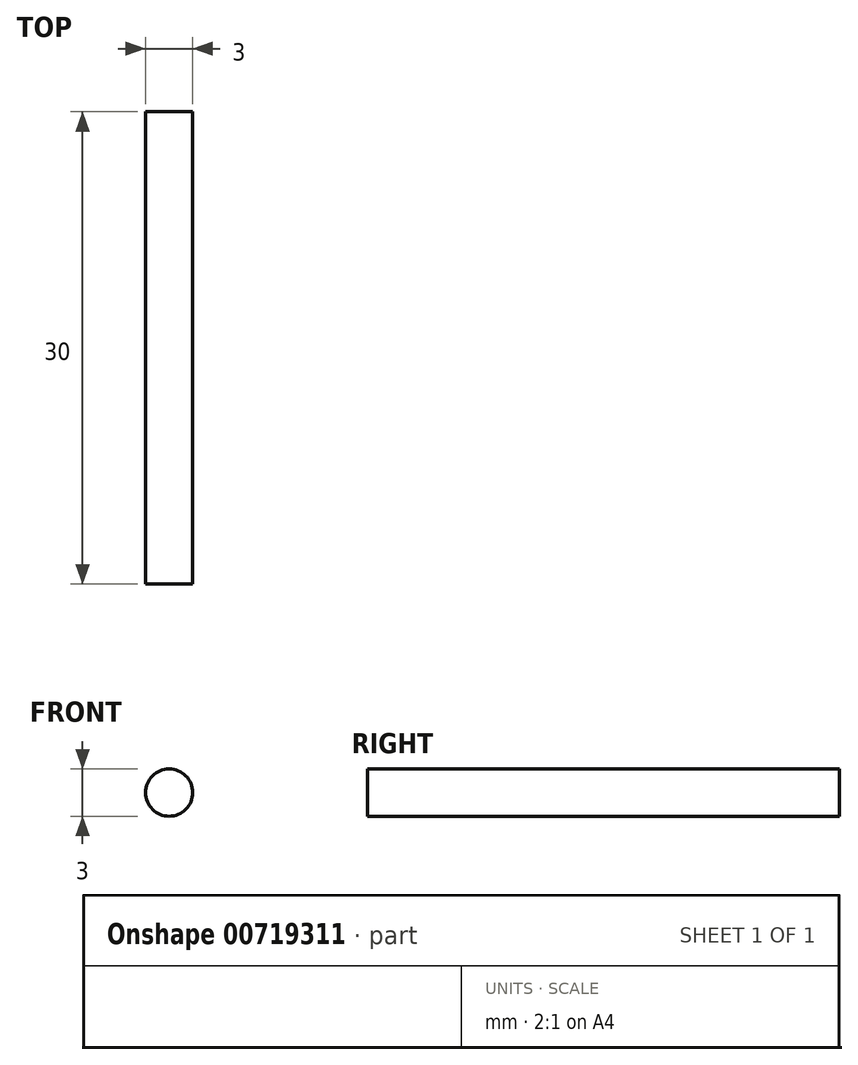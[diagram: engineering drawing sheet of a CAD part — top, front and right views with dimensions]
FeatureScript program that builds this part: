
annotation { "Feature Type Name" : "Feature", "Feature Type Description" : "" }
export const myFeature = defineFeature(function(context is Context, id is Id, definition is map)
    precondition{}
    {
        {
            var Q0;
            Q0=qCreatedBy(makeId("Front.planeOp"),FACE);
            var sketch = newSketch(context, id + "F0", { "sketchPlane" : qUnion([Q0])});
            skCircle(sketch, "E0", {"center": v(0, 0) * mm, "radius": 1.5 * mm});
            skSolve(sketch);
        }
        {
            var Q0;
            Q0=sQuery(id+"F0.wireOp",EDGE,"E0");
            extrude(context, id + "F1", {"bodyType" : ToolBodyType.SURFACE, "surfaceEntities" : qUnion([Q0]), "depth" : 30 * mm, "offsetDistance" : 25 * mm});
        }
    });
